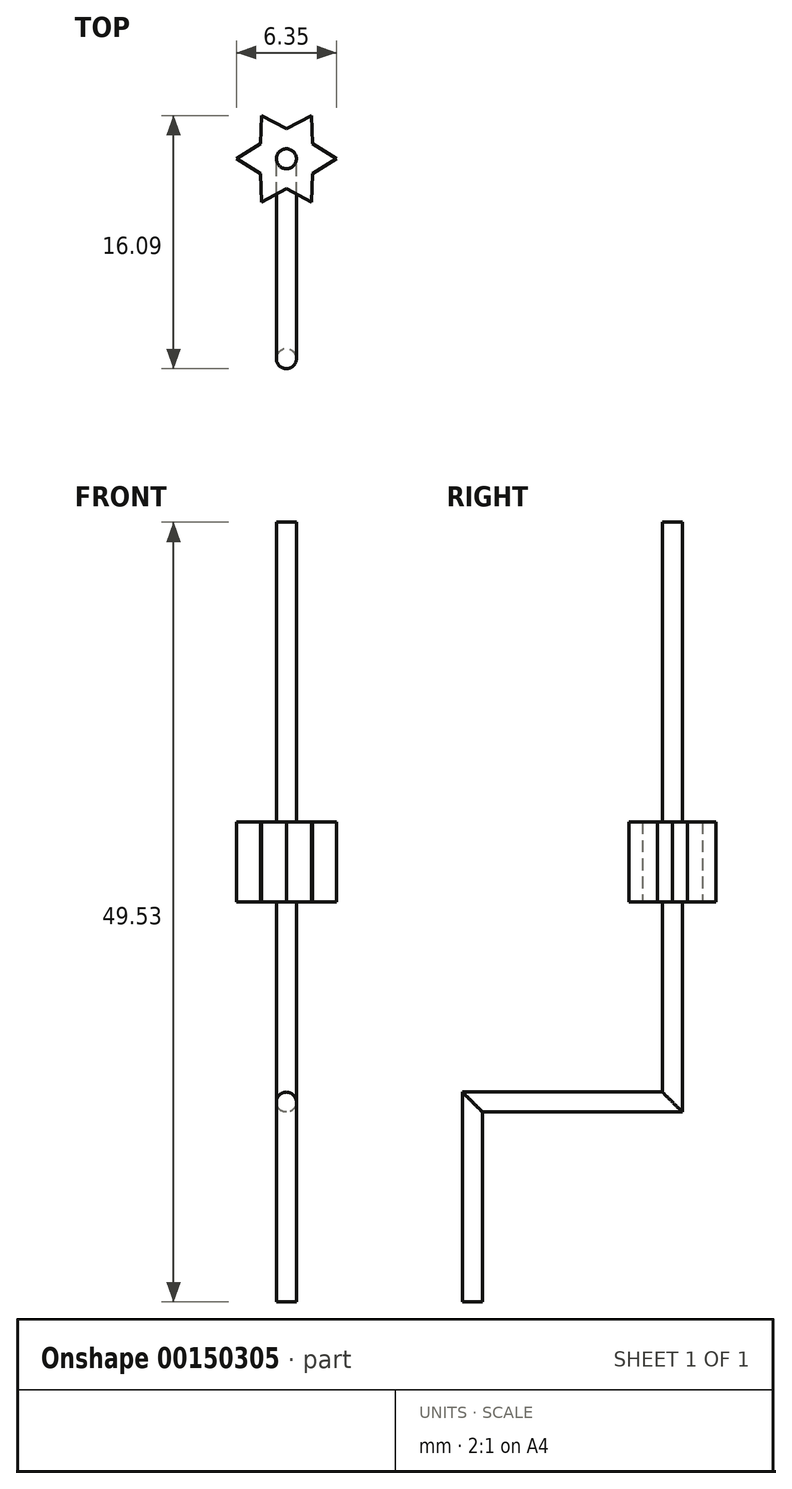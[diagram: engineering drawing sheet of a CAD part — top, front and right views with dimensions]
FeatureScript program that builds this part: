
annotation { "Feature Type Name" : "Feature", "Feature Type Description" : "" }
export const myFeature = defineFeature(function(context is Context, id is Id, definition is map)
    precondition{}
    {
        {
            var Q0;
            Q0=qCreatedBy(makeId("Top.planeOp"),FACE);
            var sketch = newSketch(context, id + "F0", { "sketchPlane" : qUnion([Q0])});
            skCircle(sketch, "E0", {"center": v(0, 0) * mm, "radius": 0.64 * mm});
            skSolve(sketch);
        }
        {
            var Q0;
            Q0=qCreatedBy(makeId("Right.planeOp"),FACE);
            var sketch = newSketch(context, id + "F1", { "sketchPlane" : qUnion([Q0])});
            skLineSegment(sketch, "E1", {"start": v(0, 0) * mm, "end": v(0, 12.7) * mm});
            skLineSegment(sketch, "E2", {"start": v(0, 12.7) * mm, "end": v(12.7, 12.7) * mm});
            skLineSegment(sketch, "E3", {"start": v(12.7, 12.7) * mm, "end": v(12.7, 25.4) * mm});
            skSolve(sketch);
        }
        {
            var Q0;
            Q0=makeQuery(id+"F0.imprint","IMPRINT",FACE,{"disambiguationData":[TD([[makeQuery(id+"F0.imprint","IMPRINT",EDGE,{"derivedFrom":sQuery(id+"F0.wireOp",EDGE,"E0")}),1.0]])]});
            var Q1;
            Q1=sQuery(id+"F1.wireOp",EDGE,"E1");
            var Q2;
            Q2=sQuery(id+"F1.wireOp",EDGE,"E2");
            var Q3;
            Q3=sQuery(id+"F1.wireOp",EDGE,"E3");
            sweep(context, id + "F2", {"profiles" : qUnion([Q0]), "path" : qUnion([Q1, Q2, Q3])});
        }
        {
            var Q0;
            Q0=makeQuery(id+"F2.opSweep","CAP_FACE",FACE,{"disambiguationData":[OSD([sQuery(id+"F0.wireOp",EDGE,"E0"),sQuery(id+"F1.wireOp",VERTEX,"E3.end")])],"isStart":false});
            var sketch = newSketch(context, id + "F3", { "sketchPlane" : qUnion([Q0])});
            skLineSegment(sketch, "E4", {"start": v(0, 0) * mm, "end": v(0, 12.7) * mm});
            skCircle(sketch, "E5", {"center": v(0, 12.7) * mm, "radius": 1.9 * mm});
            skCircle(sketch, "E6", {"center": v(0, 12.7) * mm, "radius": 3.17 * mm});
            skLineSegment(sketch, "E7", {"start": v(0, 12.7) * mm, "end": v(0, 10.8) * mm});
            skLineSegment(sketch, "E8", {"start": v(0, 10.8) * mm, "end": v(1.59, 9.95) * mm});
            skLineSegment(sketch, "E9", {"start": v(1.59, 9.95) * mm, "end": v(0, 12.7) * mm});
            skLineSegment(sketch, "E10.MirrorCS", {"start": v(0, 12.7) * mm, "end": v(1.65, 11.75) * mm});
            skLineSegment(sketch, "E11.MirrorCS", {"start": v(1.65, 11.75) * mm, "end": v(1.59, 9.95) * mm});
            skLineSegment(sketch, "E12.MirrorCS", {"start": v(1.65, 11.75) * mm, "end": v(3.18, 12.7) * mm});
            skLineSegment(sketch, "E13.MirrorCS", {"start": v(3.17, 12.7) * mm, "end": v(0, 12.7) * mm});
            skLineSegment(sketch, "E14.MirrorCS", {"start": v(0, 12.7) * mm, "end": v(1.65, 13.65) * mm});
            skLineSegment(sketch, "E15.MirrorCS", {"start": v(1.65, 13.65) * mm, "end": v(3.17, 12.7) * mm});
            skLineSegment(sketch, "E16.MirrorCS", {"start": v(0, 10.8) * mm, "end": v(-1.59, 9.95) * mm});
            skLineSegment(sketch, "E17.MirrorCS", {"start": v(-1.59, 9.95) * mm, "end": v(0, 12.7) * mm});
            skLineSegment(sketch, "E18.MirrorCS", {"start": v(-1.65, 11.75) * mm, "end": v(-1.59, 9.95) * mm});
            skLineSegment(sketch, "E19.MirrorCS", {"start": v(0, 12.7) * mm, "end": v(-1.65, 11.75) * mm});
            skLineSegment(sketch, "E20.MirrorCS", {"start": v(-1.65, 11.75) * mm, "end": v(-3.17, 12.7) * mm});
            skLineSegment(sketch, "E21.MirrorCS", {"start": v(-3.17, 12.7) * mm, "end": v(0, 12.7) * mm});
            skLineSegment(sketch, "E22.MirrorCS", {"start": v(-1.65, 13.65) * mm, "end": v(-3.18, 12.7) * mm});
            skLineSegment(sketch, "E23.MirrorCS", {"start": v(0, 12.7) * mm, "end": v(-1.65, 13.65) * mm});
            skLineSegment(sketch, "E24.MirrorCS", {"start": v(1.65, 13.65) * mm, "end": v(1.59, 15.45) * mm});
            skLineSegment(sketch, "E25.MirrorCS", {"start": v(1.59, 15.45) * mm, "end": v(0, 12.7) * mm});
            skLineSegment(sketch, "E26.MirrorCS", {"start": v(0, 14.6) * mm, "end": v(1.59, 15.45) * mm});
            skLineSegment(sketch, "E27.MirrorCS", {"start": v(0, 12.7) * mm, "end": v(0, 14.6) * mm});
            skLineSegment(sketch, "E28.MirrorCS", {"start": v(0, 14.6) * mm, "end": v(-1.59, 15.45) * mm});
            skLineSegment(sketch, "E29.MirrorCS", {"start": v(-1.59, 15.45) * mm, "end": v(0, 12.7) * mm});
            skLineSegment(sketch, "E30.MirrorCS", {"start": v(-1.65, 13.65) * mm, "end": v(-1.59, 15.45) * mm});
            skSolve(sketch);
        }
        {
            var Q0;
            {var subQ1=sQuery(id+"F3.wireOp",EDGE,"E5");var subQ3=sQuery(id+"F3.wireOp",EDGE,"E29.MirrorCS");var subQ4=makeQuery(id+"F3.imprint","INTERSECT",VERTEX,{"derivedFrom":[subQ1,subQ3]});Q0=makeQuery(id+"F3.imprint","IMPRINT",FACE,{"disambiguationData":[TD([[makeQuery(id+"F3.imprint","IMPRINT",EDGE,{"disambiguationData":[TD([[subQ4,-1.0]])],"derivedFrom":subQ3}),-1.0]])]});}
            var Q1;
            {var subQ1=sQuery(id+"F3.wireOp",EDGE,"E5");var subQ3=sQuery(id+"F3.wireOp",EDGE,"E29.MirrorCS");var subQ4=makeQuery(id+"F3.imprint","INTERSECT",VERTEX,{"derivedFrom":[subQ1,subQ3]});Q1=makeQuery(id+"F3.imprint","IMPRINT",FACE,{"disambiguationData":[TD([[makeQuery(id+"F3.imprint","IMPRINT",EDGE,{"disambiguationData":[TD([[subQ4,-1.0]])],"derivedFrom":subQ3}),1.0]])]});}
            var Q2;
            {var subQ0=sQuery(id+"F3.wireOp",EDGE,"E28.MirrorCS");Q2=makeQuery(id+"F3.imprint","IMPRINT",FACE,{"disambiguationData":[TD([[makeQuery(id+"F3.imprint","IMPRINT",EDGE,{"derivedFrom":subQ0}),1.0]])]});}
            var Q3;
            {var subQ0=sQuery(id+"F3.wireOp",EDGE,"E30.MirrorCS");Q3=makeQuery(id+"F3.imprint","IMPRINT",FACE,{"disambiguationData":[TD([[makeQuery(id+"F3.imprint","IMPRINT",EDGE,{"derivedFrom":subQ0}),-1.0]])]});}
            var Q4;
            {var subQ1=sQuery(id+"F3.wireOp",EDGE,"E27.MirrorCS");var subQ3=makeQuery(id+"F2.opSweep","CAP_EDGE",EDGE,{"disambiguationData":[OSD([sQuery(id+"F0.wireOp",EDGE,"E0"),sQuery(id+"F1.wireOp",VERTEX,"E3.end")])],"isStart":false});var subQ4=makeQuery(id+"F3.imprint","INTERSECT",VERTEX,{"derivedFrom":[subQ3,subQ1]});Q4=makeQuery(id+"F3.imprint","IMPRINT",FACE,{"disambiguationData":[TD([[makeQuery(id+"F3.imprint","IMPRINT",EDGE,{"disambiguationData":[TD([[subQ4,-1.0]])],"derivedFrom":subQ3}),1.0]])]});}
            var Q5;
            {var subQ1=sQuery(id+"F3.wireOp",EDGE,"E19.MirrorCS");var subQ3=makeQuery(id+"F2.opSweep","CAP_EDGE",EDGE,{"disambiguationData":[OSD([sQuery(id+"F0.wireOp",EDGE,"E0"),sQuery(id+"F1.wireOp",VERTEX,"E3.end")])],"isStart":false});var subQ4=makeQuery(id+"F3.imprint","INTERSECT",VERTEX,{"derivedFrom":[subQ3,subQ1]});Q5=makeQuery(id+"F3.imprint","IMPRINT",FACE,{"disambiguationData":[TD([[makeQuery(id+"F3.imprint","IMPRINT",EDGE,{"disambiguationData":[TD([[subQ4,1.0]])],"derivedFrom":subQ3}),1.0]])]});}
            var Q6;
            {var subQ1=sQuery(id+"F3.wireOp",EDGE,"E21.MirrorCS");var subQ3=makeQuery(id+"F2.opSweep","CAP_EDGE",EDGE,{"disambiguationData":[OSD([sQuery(id+"F0.wireOp",EDGE,"E0"),sQuery(id+"F1.wireOp",VERTEX,"E3.end")])],"isStart":false});var subQ4=makeQuery(id+"F3.imprint","INTERSECT",VERTEX,{"derivedFrom":[subQ3,subQ1]});Q6=makeQuery(id+"F3.imprint","IMPRINT",FACE,{"disambiguationData":[TD([[makeQuery(id+"F3.imprint","IMPRINT",EDGE,{"disambiguationData":[TD([[subQ4,1.0]])],"derivedFrom":subQ3}),1.0]])]});}
            var Q7;
            {var subQ1=sQuery(id+"F3.wireOp",EDGE,"E23.MirrorCS");var subQ3=makeQuery(id+"F2.opSweep","CAP_EDGE",EDGE,{"disambiguationData":[OSD([sQuery(id+"F0.wireOp",EDGE,"E0"),sQuery(id+"F1.wireOp",VERTEX,"E3.end")])],"isStart":false});var subQ4=makeQuery(id+"F3.imprint","INTERSECT",VERTEX,{"derivedFrom":[subQ3,subQ1]});Q7=makeQuery(id+"F3.imprint","IMPRINT",FACE,{"disambiguationData":[TD([[makeQuery(id+"F3.imprint","IMPRINT",EDGE,{"disambiguationData":[TD([[subQ4,1.0]])],"derivedFrom":subQ3}),1.0]])]});}
            var Q8;
            {var subQ1=sQuery(id+"F3.wireOp",EDGE,"E17.MirrorCS");var subQ3=makeQuery(id+"F2.opSweep","CAP_EDGE",EDGE,{"disambiguationData":[OSD([sQuery(id+"F0.wireOp",EDGE,"E0"),sQuery(id+"F1.wireOp",VERTEX,"E3.end")])],"isStart":false});var subQ4=makeQuery(id+"F3.imprint","INTERSECT",VERTEX,{"derivedFrom":[subQ3,subQ1]});Q8=makeQuery(id+"F3.imprint","IMPRINT",FACE,{"disambiguationData":[TD([[makeQuery(id+"F3.imprint","IMPRINT",EDGE,{"disambiguationData":[TD([[subQ4,1.0]])],"derivedFrom":subQ3}),1.0]])]});}
            var Q9;
            {var subQ1=sQuery(id+"F3.wireOp",EDGE,"E7");var subQ3=makeQuery(id+"F2.opSweep","CAP_EDGE",EDGE,{"disambiguationData":[OSD([sQuery(id+"F0.wireOp",EDGE,"E0"),sQuery(id+"F1.wireOp",VERTEX,"E3.end")])],"isStart":false});var subQ4=makeQuery(id+"F3.imprint","INTERSECT",VERTEX,{"derivedFrom":[subQ3,subQ1]});Q9=makeQuery(id+"F3.imprint","IMPRINT",FACE,{"disambiguationData":[TD([[makeQuery(id+"F3.imprint","IMPRINT",EDGE,{"disambiguationData":[TD([[subQ4,-1.0]])],"derivedFrom":subQ3}),1.0]])]});}
            var Q10;
            {var subQ1=sQuery(id+"F3.wireOp",EDGE,"E9");var subQ3=makeQuery(id+"F2.opSweep","CAP_EDGE",EDGE,{"disambiguationData":[OSD([sQuery(id+"F0.wireOp",EDGE,"E0"),sQuery(id+"F1.wireOp",VERTEX,"E3.end")])],"isStart":false});var subQ4=makeQuery(id+"F3.imprint","INTERSECT",VERTEX,{"derivedFrom":[subQ3,subQ1]});Q10=makeQuery(id+"F3.imprint","IMPRINT",FACE,{"disambiguationData":[TD([[makeQuery(id+"F3.imprint","IMPRINT",EDGE,{"disambiguationData":[TD([[subQ4,-1.0]])],"derivedFrom":subQ3}),1.0]])]});}
            var Q11;
            {var subQ1=sQuery(id+"F3.wireOp",EDGE,"E10.MirrorCS");var subQ3=makeQuery(id+"F2.opSweep","CAP_EDGE",EDGE,{"disambiguationData":[OSD([sQuery(id+"F0.wireOp",EDGE,"E0"),sQuery(id+"F1.wireOp",VERTEX,"E3.end")])],"isStart":false});var subQ4=makeQuery(id+"F3.imprint","INTERSECT",VERTEX,{"derivedFrom":[subQ3,subQ1]});Q11=makeQuery(id+"F3.imprint","IMPRINT",FACE,{"disambiguationData":[TD([[makeQuery(id+"F3.imprint","IMPRINT",EDGE,{"disambiguationData":[TD([[subQ4,-1.0]])],"derivedFrom":subQ3}),1.0]])]});}
            var Q12;
            {var subQ1=sQuery(id+"F3.wireOp",EDGE,"E13.MirrorCS");var subQ3=makeQuery(id+"F2.opSweep","CAP_EDGE",EDGE,{"disambiguationData":[OSD([sQuery(id+"F0.wireOp",EDGE,"E0"),sQuery(id+"F1.wireOp",VERTEX,"E3.end")])],"isStart":false});var subQ4=makeQuery(id+"F3.imprint","INTERSECT",VERTEX,{"derivedFrom":[subQ3,subQ1]});Q12=makeQuery(id+"F3.imprint","IMPRINT",FACE,{"disambiguationData":[TD([[makeQuery(id+"F3.imprint","IMPRINT",EDGE,{"disambiguationData":[TD([[subQ4,-1.0]])],"derivedFrom":subQ3}),1.0]])]});}
            var Q13;
            {var subQ1=sQuery(id+"F3.wireOp",EDGE,"E14.MirrorCS");var subQ3=makeQuery(id+"F2.opSweep","CAP_EDGE",EDGE,{"disambiguationData":[OSD([sQuery(id+"F0.wireOp",EDGE,"E0"),sQuery(id+"F1.wireOp",VERTEX,"E3.end")])],"isStart":false});var subQ4=makeQuery(id+"F3.imprint","INTERSECT",VERTEX,{"derivedFrom":[subQ3,subQ1]});Q13=makeQuery(id+"F3.imprint","IMPRINT",FACE,{"disambiguationData":[TD([[makeQuery(id+"F3.imprint","IMPRINT",EDGE,{"disambiguationData":[TD([[subQ4,-1.0]])],"derivedFrom":subQ3}),1.0]])]});}
            var Q14;
            {var subQ1=sQuery(id+"F3.wireOp",EDGE,"E25.MirrorCS");var subQ3=makeQuery(id+"F2.opSweep","CAP_EDGE",EDGE,{"disambiguationData":[OSD([sQuery(id+"F0.wireOp",EDGE,"E0"),sQuery(id+"F1.wireOp",VERTEX,"E3.end")])],"isStart":false});var subQ4=makeQuery(id+"F3.imprint","INTERSECT",VERTEX,{"derivedFrom":[subQ3,subQ1]});Q14=makeQuery(id+"F3.imprint","IMPRINT",FACE,{"disambiguationData":[TD([[makeQuery(id+"F3.imprint","IMPRINT",EDGE,{"disambiguationData":[TD([[subQ4,-1.0]])],"derivedFrom":subQ3}),1.0]])]});}
            var Q15;
            {var subQ1=sQuery(id+"F3.wireOp",EDGE,"E7");var subQ3=makeQuery(id+"F2.opSweep","CAP_EDGE",EDGE,{"disambiguationData":[OSD([sQuery(id+"F0.wireOp",EDGE,"E0"),sQuery(id+"F1.wireOp",VERTEX,"E3.end")])],"isStart":false});var subQ4=makeQuery(id+"F3.imprint","INTERSECT",VERTEX,{"derivedFrom":[subQ3,subQ1]});Q15=makeQuery(id+"F3.imprint","IMPRINT",FACE,{"disambiguationData":[TD([[makeQuery(id+"F3.imprint","IMPRINT",EDGE,{"disambiguationData":[TD([[subQ4,1.0]])],"derivedFrom":subQ3}),1.0]])]});}
            var Q16;
            {var subQ1=sQuery(id+"F3.wireOp",EDGE,"E5");var subQ3=sQuery(id+"F3.wireOp",EDGE,"E25.MirrorCS");var subQ4=makeQuery(id+"F3.imprint","INTERSECT",VERTEX,{"derivedFrom":[subQ1,subQ3]});Q16=makeQuery(id+"F3.imprint","IMPRINT",FACE,{"disambiguationData":[TD([[makeQuery(id+"F3.imprint","IMPRINT",EDGE,{"disambiguationData":[TD([[subQ4,-1.0]])],"derivedFrom":subQ3}),-1.0]])]});}
            var Q17;
            {var subQ1=sQuery(id+"F3.wireOp",EDGE,"E5");var subQ3=sQuery(id+"F3.wireOp",EDGE,"E25.MirrorCS");var subQ4=makeQuery(id+"F3.imprint","INTERSECT",VERTEX,{"derivedFrom":[subQ1,subQ3]});Q17=makeQuery(id+"F3.imprint","IMPRINT",FACE,{"disambiguationData":[TD([[makeQuery(id+"F3.imprint","IMPRINT",EDGE,{"disambiguationData":[TD([[subQ4,-1.0]])],"derivedFrom":subQ3}),1.0]])]});}
            var Q18;
            {var subQ0=sQuery(id+"F3.wireOp",EDGE,"E26.MirrorCS");Q18=makeQuery(id+"F3.imprint","IMPRINT",FACE,{"disambiguationData":[TD([[makeQuery(id+"F3.imprint","IMPRINT",EDGE,{"derivedFrom":subQ0}),-1.0]])]});}
            var Q19;
            {var subQ0=sQuery(id+"F3.wireOp",EDGE,"E24.MirrorCS");Q19=makeQuery(id+"F3.imprint","IMPRINT",FACE,{"disambiguationData":[TD([[makeQuery(id+"F3.imprint","IMPRINT",EDGE,{"derivedFrom":subQ0}),1.0]])]});}
            var Q20;
            {var subQ1=sQuery(id+"F3.wireOp",EDGE,"E5");var subQ3=sQuery(id+"F3.wireOp",EDGE,"E13.MirrorCS");var subQ4=makeQuery(id+"F3.imprint","INTERSECT",VERTEX,{"derivedFrom":[subQ1,subQ3]});Q20=makeQuery(id+"F3.imprint","IMPRINT",FACE,{"disambiguationData":[TD([[makeQuery(id+"F3.imprint","IMPRINT",EDGE,{"disambiguationData":[TD([[subQ4,-1.0]])],"derivedFrom":subQ3}),-1.0]])]});}
            var Q21;
            {var subQ1=sQuery(id+"F3.wireOp",EDGE,"E5");var subQ3=sQuery(id+"F3.wireOp",EDGE,"E13.MirrorCS");var subQ4=makeQuery(id+"F3.imprint","INTERSECT",VERTEX,{"derivedFrom":[subQ1,subQ3]});Q21=makeQuery(id+"F3.imprint","IMPRINT",FACE,{"disambiguationData":[TD([[makeQuery(id+"F3.imprint","IMPRINT",EDGE,{"disambiguationData":[TD([[subQ4,-1.0]])],"derivedFrom":subQ3}),1.0]])]});}
            var Q22;
            {var subQ1=sQuery(id+"F3.wireOp",EDGE,"E5");var subQ3=sQuery(id+"F3.wireOp",EDGE,"E9");var subQ4=makeQuery(id+"F3.imprint","INTERSECT",VERTEX,{"derivedFrom":[subQ1,subQ3]});Q22=makeQuery(id+"F3.imprint","IMPRINT",FACE,{"disambiguationData":[TD([[makeQuery(id+"F3.imprint","IMPRINT",EDGE,{"disambiguationData":[TD([[subQ4,-1.0]])],"derivedFrom":subQ3}),-1.0]])]});}
            var Q23;
            {var subQ1=sQuery(id+"F3.wireOp",EDGE,"E5");var subQ3=sQuery(id+"F3.wireOp",EDGE,"E9");var subQ4=makeQuery(id+"F3.imprint","INTERSECT",VERTEX,{"derivedFrom":[subQ1,subQ3]});Q23=makeQuery(id+"F3.imprint","IMPRINT",FACE,{"disambiguationData":[TD([[makeQuery(id+"F3.imprint","IMPRINT",EDGE,{"disambiguationData":[TD([[subQ4,-1.0]])],"derivedFrom":subQ3}),1.0]])]});}
            var Q24;
            {var subQ1=sQuery(id+"F3.wireOp",EDGE,"E5");var subQ3=sQuery(id+"F3.wireOp",EDGE,"E17.MirrorCS");var subQ4=makeQuery(id+"F3.imprint","INTERSECT",VERTEX,{"derivedFrom":[subQ1,subQ3]});Q24=makeQuery(id+"F3.imprint","IMPRINT",FACE,{"disambiguationData":[TD([[makeQuery(id+"F3.imprint","IMPRINT",EDGE,{"disambiguationData":[TD([[subQ4,-1.0]])],"derivedFrom":subQ3}),-1.0]])]});}
            var Q25;
            {var subQ1=sQuery(id+"F3.wireOp",EDGE,"E5");var subQ3=sQuery(id+"F3.wireOp",EDGE,"E17.MirrorCS");var subQ4=makeQuery(id+"F3.imprint","INTERSECT",VERTEX,{"derivedFrom":[subQ1,subQ3]});Q25=makeQuery(id+"F3.imprint","IMPRINT",FACE,{"disambiguationData":[TD([[makeQuery(id+"F3.imprint","IMPRINT",EDGE,{"disambiguationData":[TD([[subQ4,-1.0]])],"derivedFrom":subQ3}),1.0]])]});}
            var Q26;
            {var subQ1=sQuery(id+"F3.wireOp",EDGE,"E5");var subQ3=sQuery(id+"F3.wireOp",EDGE,"E21.MirrorCS");var subQ4=makeQuery(id+"F3.imprint","INTERSECT",VERTEX,{"derivedFrom":[subQ1,subQ3]});Q26=makeQuery(id+"F3.imprint","IMPRINT",FACE,{"disambiguationData":[TD([[makeQuery(id+"F3.imprint","IMPRINT",EDGE,{"disambiguationData":[TD([[subQ4,-1.0]])],"derivedFrom":subQ3}),-1.0]])]});}
            var Q27;
            {var subQ1=sQuery(id+"F3.wireOp",EDGE,"E5");var subQ3=sQuery(id+"F3.wireOp",EDGE,"E21.MirrorCS");var subQ4=makeQuery(id+"F3.imprint","INTERSECT",VERTEX,{"derivedFrom":[subQ1,subQ3]});Q27=makeQuery(id+"F3.imprint","IMPRINT",FACE,{"disambiguationData":[TD([[makeQuery(id+"F3.imprint","IMPRINT",EDGE,{"disambiguationData":[TD([[subQ4,-1.0]])],"derivedFrom":subQ3}),1.0]])]});}
            var Q28;
            {var subQ0=sQuery(id+"F3.wireOp",EDGE,"E22.MirrorCS");Q28=makeQuery(id+"F3.imprint","IMPRINT",FACE,{"disambiguationData":[TD([[makeQuery(id+"F3.imprint","IMPRINT",EDGE,{"derivedFrom":subQ0}),1.0]])]});}
            var Q29;
            {var subQ0=sQuery(id+"F3.wireOp",EDGE,"E20.MirrorCS");Q29=makeQuery(id+"F3.imprint","IMPRINT",FACE,{"disambiguationData":[TD([[makeQuery(id+"F3.imprint","IMPRINT",EDGE,{"derivedFrom":subQ0}),-1.0]])]});}
            var Q30;
            {var subQ0=sQuery(id+"F3.wireOp",EDGE,"E18.MirrorCS");Q30=makeQuery(id+"F3.imprint","IMPRINT",FACE,{"disambiguationData":[TD([[makeQuery(id+"F3.imprint","IMPRINT",EDGE,{"derivedFrom":subQ0}),1.0]])]});}
            var Q31;
            {var subQ0=sQuery(id+"F3.wireOp",EDGE,"E16.MirrorCS");Q31=makeQuery(id+"F3.imprint","IMPRINT",FACE,{"disambiguationData":[TD([[makeQuery(id+"F3.imprint","IMPRINT",EDGE,{"derivedFrom":subQ0}),-1.0]])]});}
            var Q32;
            {var subQ0=sQuery(id+"F3.wireOp",EDGE,"E8");Q32=makeQuery(id+"F3.imprint","IMPRINT",FACE,{"disambiguationData":[TD([[makeQuery(id+"F3.imprint","IMPRINT",EDGE,{"derivedFrom":subQ0}),1.0]])]});}
            var Q33;
            {var subQ0=sQuery(id+"F3.wireOp",EDGE,"E11.MirrorCS");Q33=makeQuery(id+"F3.imprint","IMPRINT",FACE,{"disambiguationData":[TD([[makeQuery(id+"F3.imprint","IMPRINT",EDGE,{"derivedFrom":subQ0}),-1.0]])]});}
            var Q34;
            {var subQ0=sQuery(id+"F3.wireOp",EDGE,"E12.MirrorCS");Q34=makeQuery(id+"F3.imprint","IMPRINT",FACE,{"disambiguationData":[TD([[makeQuery(id+"F3.imprint","IMPRINT",EDGE,{"derivedFrom":subQ0}),1.0]])]});}
            var Q35;
            {var subQ0=sQuery(id+"F3.wireOp",EDGE,"E15.MirrorCS");Q35=makeQuery(id+"F3.imprint","IMPRINT",FACE,{"disambiguationData":[TD([[makeQuery(id+"F3.imprint","IMPRINT",EDGE,{"derivedFrom":subQ0}),-1.0]])]});}
            extrude(context, id + "F4", {"entities" : qUnion([Q0, Q1, Q2, Q3, Q4, Q5, Q6, Q7, Q8, Q9, Q10, Q11, Q12, Q13, Q14, Q15, Q16, Q17, Q18, Q19, Q20, Q21, Q22, Q23, Q24, Q25, Q26, Q27, Q28, Q29, Q30, Q31, Q32, Q33, Q34, Q35]), "operationType" : NewBodyOperationType.ADD, "depth" : 5.08 * mm});
        }
        {
            var Q0;
            Q0=makeQuery(id+"F4.opExtrude","CAP_FACE",FACE,{"disambiguationData":[OSD([sQuery(id+"F3.wireOp",EDGE,"E8"),sQuery(id+"F3.wireOp",EDGE,"E11.MirrorCS"),sQuery(id+"F3.wireOp",EDGE,"E12.MirrorCS"),sQuery(id+"F3.wireOp",EDGE,"E15.MirrorCS"),sQuery(id+"F3.wireOp",EDGE,"E16.MirrorCS"),sQuery(id+"F3.wireOp",EDGE,"E18.MirrorCS"),sQuery(id+"F3.wireOp",EDGE,"E20.MirrorCS"),sQuery(id+"F3.wireOp",EDGE,"E22.MirrorCS"),sQuery(id+"F3.wireOp",EDGE,"E24.MirrorCS"),sQuery(id+"F3.wireOp",EDGE,"E26.MirrorCS"),sQuery(id+"F3.wireOp",EDGE,"E28.MirrorCS"),sQuery(id+"F3.wireOp",EDGE,"E30.MirrorCS")])],"isStart":false});
            var sketch = newSketch(context, id + "F5", { "sketchPlane" : qUnion([Q0])});
            skLineSegment(sketch, "E31", {"start": v(0, 0) * mm, "end": v(0, 12.7) * mm});
            skLineSegment(sketch, "E32", {"start": v(0, 12.7) * mm, "end": v(3.18, 12.7) * mm});
            skCircle(sketch, "E33", {"center": v(0, 12.7) * mm, "radius": 0.64 * mm});
            skSolve(sketch);
        }
        {
            var Q0;
            Q0 = qSketchRegion(id + "F5", true);
            extrude(context, id + "F6", {"entities" : qUnion([Q0]), "operationType" : NewBodyOperationType.ADD, "depth" : 19.05 * mm});
        }
    });
